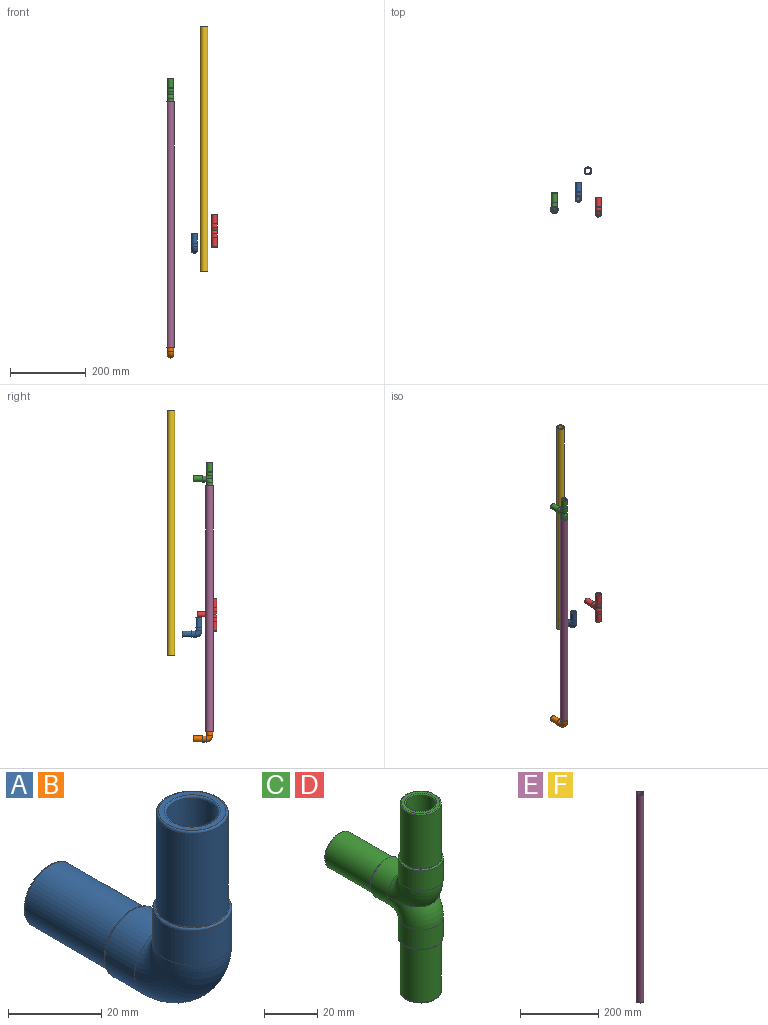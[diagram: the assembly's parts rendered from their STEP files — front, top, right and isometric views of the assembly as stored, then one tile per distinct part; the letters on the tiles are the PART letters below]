
ASSEMBLY  parts=6 mates=2
PART A: 18 faces, bbox 18.4x53.4x53.4 mm
  f0: plane 16x16mm, normal (0,1,0), area 12.4mm2, adj f5,f15
  f1: plane 16x16mm, normal (0,0,1), area 12.4mm2, adj f7,f14
  f2: cylinder r=8.5mm len=17mm, axis (0,-1,0), area 480.7mm2, adj f3,f15
  f3: torus R=9mm, axis (-1,0,0), area 755mm2, adj f2,f4
  f4: cylinder r=8.5mm len=17mm, axis (0,0,1), area 480.7mm2, adj f3,f14
  f5: cylinder r=7.75mm len=24.5mm, axis (0,-1,0), area 1193mm2, adj f0,f13
  f6: plane 14.5x14.5mm, normal (0,1,0), area 52mm2, adj f13,f17
  f7: cylinder r=7.75mm len=24.5mm, axis (0,0,-1), area 1193mm2, adj f1,f12
  f8: plane 14.5x14.5mm, normal (0,0,1), area 52mm2, adj f12,f16
  f9: cylinder r=5.5mm len=34mm, axis (0,-1,0), area 1175mm2, adj f10,f17
  f10: torus R=9mm, axis (-1,0,0), area 488.5mm2, adj f9,f11
  f11: cylinder r=5.5mm len=34mm, axis (0,0,1), area 1175mm2, adj f10,f16
  f12: torus R=7.25mm, axis (0,0,1), area 37.3mm2, adj f7,f8
  f13: torus R=7.25mm, axis (0,1,0), area 37.3mm2, adj f5,f6
  f14: torus R=8mm, axis (0,0,1), area 41mm2, adj f1,f4
  f15: torus R=8mm, axis (0,-1,0), area 41mm2, adj f0,f2
  f16: torus R=6mm, axis (0,0,1), area 28mm2, adj f8,f11
  f17: torus R=6mm, axis (0,1,0), area 28mm2, adj f6,f9
PART B: same geometry as A
PART C: 32 faces, bbox 18.4x53.4x87 mm
  f0: torus R=9mm, axis (-1,0,0), area 161.7mm2, adj f10,f19
  f1: plane 16x16mm, normal (0,1,0), area 12.4mm2, adj f6,f16
  f2: plane 16x16mm, normal (0,0,1), area 12.4mm2, adj f8,f15
  f3: cylinder r=8.5mm len=17mm, axis (0,-1,0), area 480.7mm2, adj f4,f16,f22
  f4: torus R=9mm, axis (-1,0,0), area 416.4mm2, adj f3,f5,f22
  f5: cylinder r=8.5mm len=17mm, axis (0,0,1), area 480.7mm2, adj f4,f15
  f6: cylinder r=7.75mm len=24.5mm, axis (0,-1,0), area 1193mm2, adj f1,f14
  f7: plane 14.5x14.5mm, normal (0,1,0), area 52mm2, adj f14,f18
  f8: cylinder r=7.75mm len=24.5mm, axis (0,0,-1), area 1193mm2, adj f2,f13
  f9: plane 14.5x14.5mm, normal (0,0,1), area 52mm2, adj f13,f17
  f10: cylinder r=5.5mm len=34mm, axis (0,-1,0), area 1175mm2, adj f0,f18,f19
  f11: torus R=9mm, axis (-1,0,0), area 146.3mm2, adj f12,f20
  f12: cylinder r=5.5mm len=34mm, axis (0,0,1), area 1175mm2, adj f11,f17
  f13: torus R=7.25mm, axis (0,0,1), area 37.3mm2, adj f8,f9
  f14: torus R=7.25mm, axis (0,1,0), area 37.3mm2, adj f6,f7
  f15: torus R=8mm, axis (0,0,1), area 41mm2, adj f2,f5
  f16: torus R=8mm, axis (0,-1,0), area 41mm2, adj f1,f3
  f17: torus R=6mm, axis (0,0,1), area 28mm2, adj f9,f12
  f18: torus R=6mm, axis (0,1,0), area 28mm2, adj f7,f10
  f19: torus R=9mm, axis (-1,0,0), area 161.7mm2, adj f0,f10
  f20: torus R=9mm, axis (-1,0,0), area 103mm2, adj f11
  f21: plane 16x16mm, normal (0,0,-1), area 12.4mm2, adj f24,f29
  f22: torus R=9mm, axis (-1,0,0), area 416.4mm2, adj f3,f4,f23
  f23: cylinder r=8.5mm len=17mm, axis (0,0,-1), area 480.7mm2, adj f22,f29
  f24: cylinder r=7.75mm len=24.5mm, axis (0,0,1), area 1193mm2, adj f21,f28
  f25: plane 14.5x14.5mm, normal (0,0,-1), area 52mm2, adj f28,f30
  f26: torus R=9mm, axis (-1,0,0), area 146.3mm2, adj f27,f31
  f27: cylinder r=5.5mm len=34mm, axis (0,0,-1), area 1175mm2, adj f26,f30
  f28: torus R=7.25mm, axis (0,0,-1), area 37.3mm2, adj f24,f25
  f29: torus R=8mm, axis (0,0,-1), area 41mm2, adj f21,f23
  f30: torus R=6mm, axis (0,0,-1), area 28mm2, adj f25,f27
  f31: torus R=9mm, axis (-1,0,0), area 102.9mm2, adj f26
PART D: same geometry as C
PART E: 4 faces, bbox 20x20x650 mm
  f0: cylinder r=7.85mm len=650mm, axis (0,0,-1), area 32060mm2, adj f2,f3
  f1: cylinder r=10mm len=650mm, axis (0,0,-1), area 40840.7mm2, adj f2,f3
  f2: plane 20x20mm, normal (0,0,1), area 120.6mm2, adj f0,f1
  f3: plane 20x20mm, normal (0,0,-1), area 120.6mm2, adj f0,f1
PART F: same geometry as E
PLACE A t=(79.67,50.45,111.73)mm
PLACE B t=(16.05,22.07,-164.99)mm fixed
PLACE C t=(16.05,22.07,522.01)mm
PLACE D t=(132.19,10.99,163.29)mm
PLACE E t=(16.05,22.07,-146.49)mm
PLACE F t=(105.09,124.09,53.91)mm
MATE fastened E.f1 <-> B.f4  axis (0,0,-1) through (16.05,22.07,-146.49)mm
MATE fastened E.f1 <-> C.f5  axis (0,0,1) through (16.05,22.07,503.51)mm
